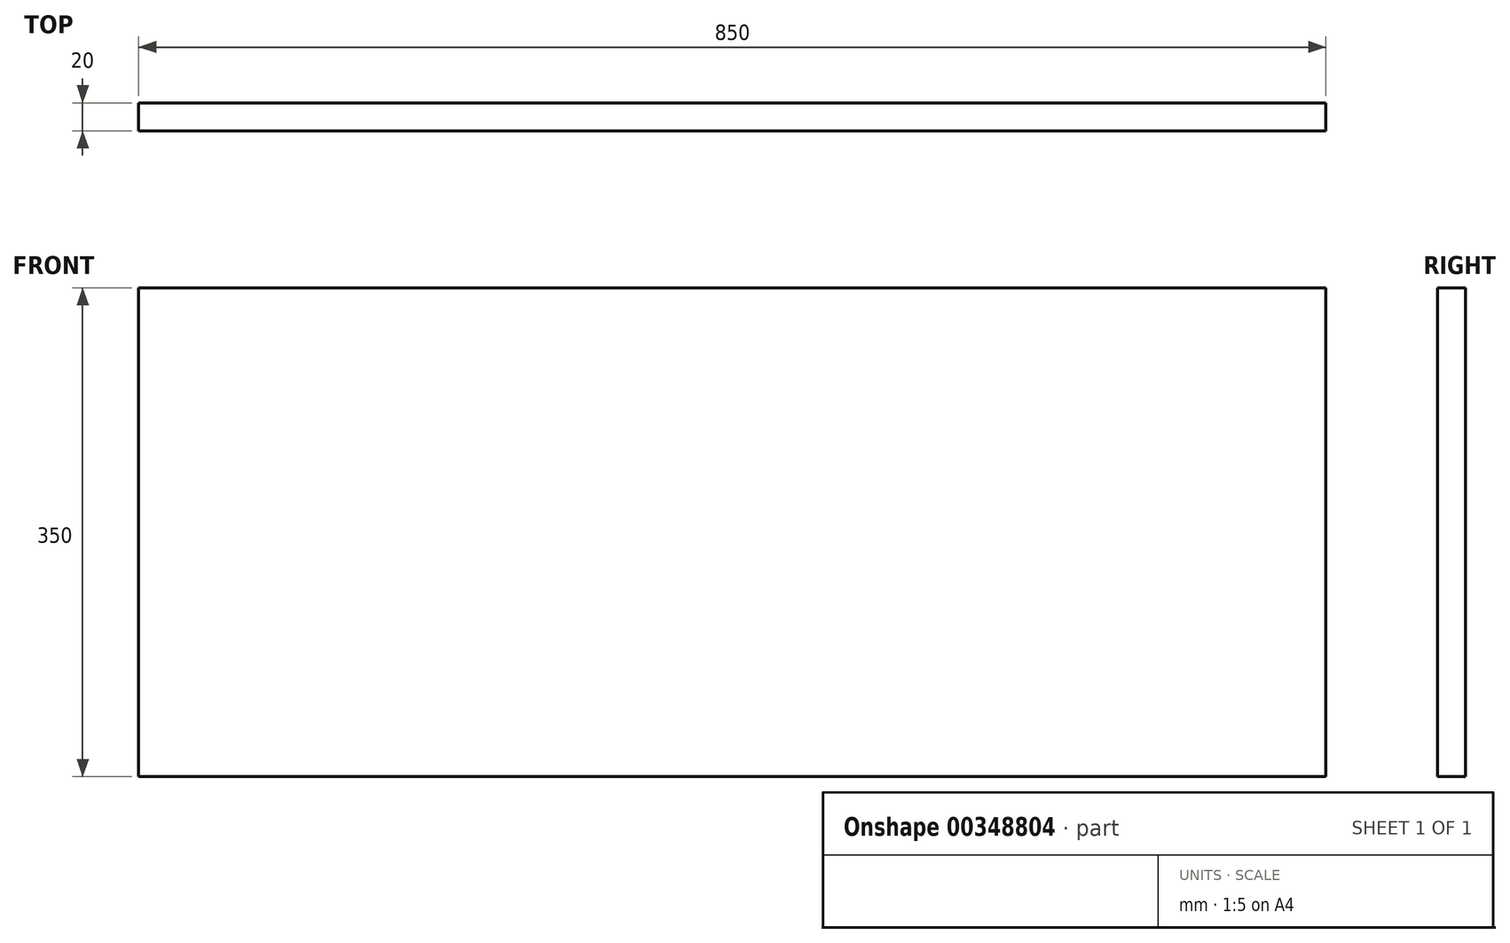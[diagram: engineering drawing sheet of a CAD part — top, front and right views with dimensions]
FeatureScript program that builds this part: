
annotation { "Feature Type Name" : "Feature", "Feature Type Description" : "" }
export const myFeature = defineFeature(function(context is Context, id is Id, definition is map)
    precondition{}
    {
        {
            var Q0;
            Q0=qCreatedBy(makeId("Front.planeOp"),FACE);
            var sketch = newSketch(context, id + "F0", { "sketchPlane" : qUnion([Q0])});
            skLineSegment(sketch, "E0.bottom", {"start": v(-850, -350) * mm, "end": v(0, -350) * mm});
            skLineSegment(sketch, "E0.top", {"start": v(-850, 0) * mm, "end": v(0, 0) * mm});
            skLineSegment(sketch, "E0.left", {"start": v(-850, -350) * mm, "end": v(-850, 0) * mm});
            skLineSegment(sketch, "E0.right", {"start": v(0, -350) * mm, "end": v(0, 0) * mm});
            skSolve(sketch);
        }
        {
            var Q0;
            Q0=qSketchRegion(id+"F0",true);
            extrude(context, id + "F1", {"entities" : qUnion([Q0]), "depth" : 20 * mm});
        }
    });
